# Revit family: Shower_Base-Acorn-Terrazzo_Ware-SBBOD-36-FF
name_source: partatom
category: Plumbing Fixtures
units: mm (PartAtom-declared; Revit-internal decimal feet)

## family parameters
Cut with Voids When Loaded = No
Host = Face
OmniClass Number = 23.45.05.14.17
OmniClass Title = Showers
Part Type = Normal
Room Calculation Point = No
Round Connector Dimension = Use Diameter
Shared = Yes

## types (1)
- SBBOD-36-FF
    ADA Compliant = Yes
    Assembly Code = D2010710
    Body Material = Portland_Cement-Acorn-Terrazzo
    CW Connection = No
    CWFU = 3
    Default Elevation = 0"
    Description = 36in. x 36in. Terrazzo Shower Base, Back Drain, 4-Flange
    HW Connection = No
    HWFU = 3
    Height = 4 1/2"
    Installation Type = Floor Mounted
    Length = 36"
    Manufacturer = Acorn Engineering
    Model = SBBOD-36-FF
    Product Documentation Link = https://www.acorneng.com
    Product Page URL = https://www.acorneng.com
    Tiling Flange Material = Metal-Acorn-Stainless Steel
    URL = https://www.acorneng.com
    VRS - Vandal Resistant Strainer = No
    Vent Connection = No
    WFU = 4
    Waste Connection = Yes
    Waste Connection Diameter = 2"
    Waste Connection Height = 1/2"
    Width = 36"
    Working Pressure = 3,000 PSI min.

## geometry (parser evidence)
native form markers: Sweep x3
no freeform markers — native parametric forms only
